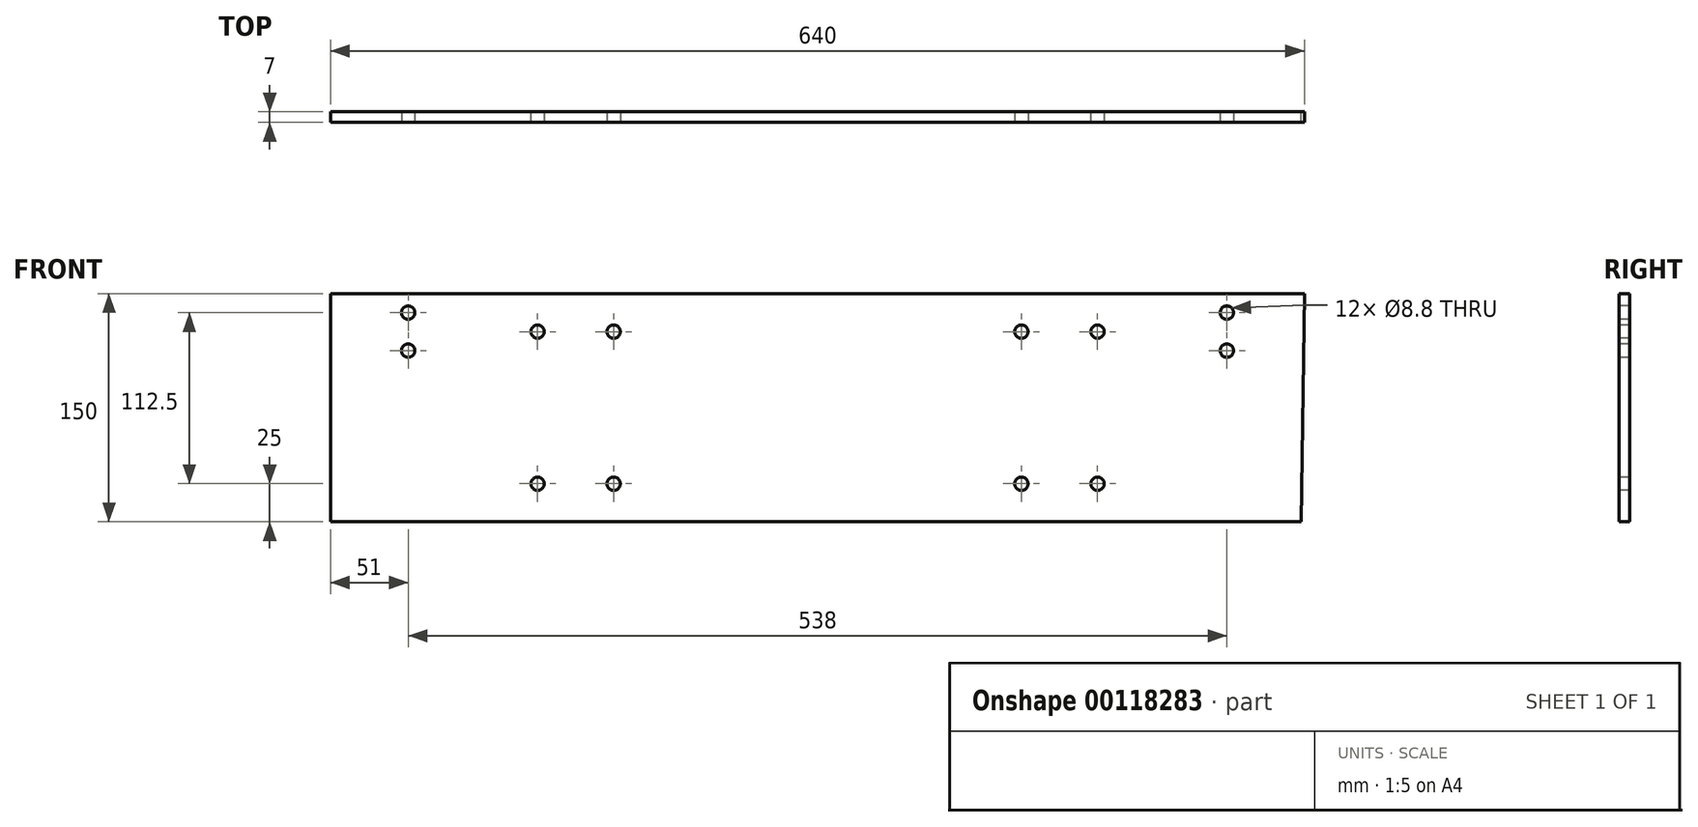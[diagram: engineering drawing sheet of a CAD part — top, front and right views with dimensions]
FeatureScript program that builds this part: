
annotation { "Feature Type Name" : "Feature", "Feature Type Description" : "" }
export const myFeature = defineFeature(function(context is Context, id is Id, definition is map)
    precondition{}
    {
        {
            var Q0;
            Q0=qCreatedBy(makeId("Front.planeOp"),FACE);
            var sketch = newSketch(context, id + "F0", { "sketchPlane" : qUnion([Q0])});
            skLineSegment(sketch, "E0.top", {"start": v(319, -450) * mm, "end": v(-319, -450) * mm});
            skPoint(sketch, "E0.middle", {"position": v(0, 0) * mm});
            skLineSegment(sketch, "E1", {"start": v(-319, -450) * mm, "end": v(-319, -300) * mm});
            skLineSegment(sketch, "E2", {"start": v(-319, -300) * mm, "end": v(321, -300) * mm});
            skLineSegment(sketch, "E3", {"start": v(321, -300) * mm, "end": v(319, -450) * mm});
            skLineSegment(sketch, "E4", {"start": v(-319, -300) * mm, "end": v(-308, -300) * mm});
            skLineSegment(sketch, "E5", {"start": v(-308, -300) * mm, "end": v(-308, -450) * mm});
            skLineSegment(sketch, "E6", {"start": v(321, -300) * mm, "end": v(310, -300) * mm});
            skLineSegment(sketch, "E7", {"start": v(310, -300) * mm, "end": v(310, -450) * mm});
            skSolve(sketch);
        }
        {
            var Q0;
            Q0=makeQuery(id+"F0.imprint","IMPRINT",FACE,{"disambiguationData":[TD([[makeQuery(id+"F0.imprint","IMPRINT",EDGE,{"derivedFrom":sQuery(id+"F0.wireOp",EDGE,"E2")}),-1.0]])]});
            extrude(context, id + "F1", {"entities" : qUnion([Q0]), "depth" : 7 * mm});
        }
        {
            var Q0;
            Q0=makeQuery(id+"F1.opExtrude","CAP_FACE",FACE,{"disambiguationData":[OSD([sQuery(id+"F0.wireOp",EDGE,"E0.top"),sQuery(id+"F0.wireOp",EDGE,"E2"),sQuery(id+"F0.wireOp",EDGE,"E5"),sQuery(id+"F0.wireOp",EDGE,"E7")])],"isStart":false});
            var sketch = newSketch(context, id + "F2", { "sketchPlane" : qUnion([Q0])});
            skLineSegment(sketch, "E8", {"start": v(-308, -300) * mm, "end": v(-158, -300) * mm});
            skLineSegment(sketch, "E9", {"start": v(310, -300) * mm, "end": v(160, -300) * mm});
            skLineSegment(sketch, "E10", {"start": v(160, -300) * mm, "end": v(-158, -300) * mm});
            skLineSegment(sketch, "E11.MirrorCS", {"start": v(198, -300) * mm, "end": v(-208, -300) * mm});
            skLineSegment(sketch, "E12.MirrorCS", {"start": v(-308, -300) * mm, "end": v(-208, -300) * mm});
            skLineSegment(sketch, "E13", {"start": v(-158, -300) * mm, "end": v(-158, -450) * mm});
            skLineSegment(sketch, "E14", {"start": v(-158, -450) * mm, "end": v(-208, -450) * mm});
            skLineSegment(sketch, "E15", {"start": v(-158, -450) * mm, "end": v(-128, -450) * mm});
            skLineSegment(sketch, "E16.bottom", {"start": v(-208, -450) * mm, "end": v(-108, -450) * mm});
            skLineSegment(sketch, "E16.top", {"start": v(-208, -400) * mm, "end": v(-108, -400) * mm});
            skLineSegment(sketch, "E16.left", {"start": v(-208, -450) * mm, "end": v(-208, -400) * mm});
            skLineSegment(sketch, "E16.right", {"start": v(-108, -450) * mm, "end": v(-108, -400) * mm});
            skLineSegment(sketch, "E17", {"start": v(-158, -450) * mm, "end": v(-108, -400) * mm});
            skLineSegment(sketch, "E18", {"start": v(-158, -300) * mm, "end": v(-158, -350) * mm});
            skLineSegment(sketch, "E19", {"start": v(-158, -350) * mm, "end": v(-208, -350) * mm});
            skLineSegment(sketch, "E20", {"start": v(-208, -350) * mm, "end": v(-158, -300) * mm});
            skLineSegment(sketch, "E21", {"start": v(-158, -300) * mm, "end": v(-108, -300) * mm});
            skLineSegment(sketch, "E22", {"start": v(-108, -300) * mm, "end": v(-108, -350) * mm});
            skLineSegment(sketch, "E23", {"start": v(-208, -350) * mm, "end": v(-208, -300) * mm});
            skLineSegment(sketch, "E24", {"start": v(-108, -350) * mm, "end": v(-158, -350) * mm});
            skLineSegment(sketch, "E25", {"start": v(-158, -350) * mm, "end": v(-108, -300) * mm});
            skLineSegment(sketch, "E26", {"start": v(-208, -450) * mm, "end": v(-158, -400) * mm});
            skLineSegment(sketch, "E27", {"start": v(160, -300) * mm, "end": v(160, -450) * mm});
            skLineSegment(sketch, "E28", {"start": v(160, -450) * mm, "end": v(160, -400) * mm});
            skLineSegment(sketch, "E29", {"start": v(160, -400) * mm, "end": v(210, -400) * mm});
            skLineSegment(sketch, "E30", {"start": v(210, -400) * mm, "end": v(210, -450) * mm});
            skLineSegment(sketch, "E31", {"start": v(160, -450) * mm, "end": v(210, -400) * mm});
            skLineSegment(sketch, "E32", {"start": v(160, -400) * mm, "end": v(110, -400) * mm});
            skLineSegment(sketch, "E33", {"start": v(110, -400) * mm, "end": v(110, -450) * mm});
            skLineSegment(sketch, "E34", {"start": v(110, -450) * mm, "end": v(160, -400) * mm});
            skLineSegment(sketch, "E35", {"start": v(160, -300) * mm, "end": v(160, -350) * mm});
            skLineSegment(sketch, "E36", {"start": v(160, -350) * mm, "end": v(160, -350) * mm});
            skLineSegment(sketch, "E37", {"start": v(160, -350) * mm, "end": v(160, -300) * mm});
            skLineSegment(sketch, "E38", {"start": v(160, -300) * mm, "end": v(210, -300) * mm});
            skLineSegment(sketch, "E39", {"start": v(210, -300) * mm, "end": v(210, -350) * mm});
            skLineSegment(sketch, "E40", {"start": v(210, -350) * mm, "end": v(160, -350) * mm});
            skLineSegment(sketch, "E41", {"start": v(210, -300) * mm, "end": v(160, -350) * mm});
            skLineSegment(sketch, "E42", {"start": v(160, -450) * mm, "end": v(135, -425) * mm});
            skLineSegment(sketch, "E43", {"start": v(-158, -450) * mm, "end": v(-183, -425) * mm});
            skLineSegment(sketch, "E44", {"start": v(-158, -350) * mm, "end": v(-183, -325) * mm});
            skLineSegment(sketch, "E45", {"start": v(160, -350) * mm, "end": v(160, -325) * mm});
            skLineSegment(sketch, "E46", {"start": v(210, -350) * mm, "end": v(185, -325) * mm});
            skLineSegment(sketch, "E47", {"start": v(210, -450) * mm, "end": v(185, -425) * mm});
            skLineSegment(sketch, "E48", {"start": v(-108, -450) * mm, "end": v(-133, -425) * mm});
            skLineSegment(sketch, "E49", {"start": v(-108, -350) * mm, "end": v(-133, -325) * mm});
            skLineSegment(sketch, "E50", {"start": v(160, -300) * mm, "end": v(110, -300) * mm});
            skLineSegment(sketch, "E51", {"start": v(160, -350) * mm, "end": v(110, -350) * mm});
            skLineSegment(sketch, "E52", {"start": v(110, -350) * mm, "end": v(110, -300) * mm});
            skLineSegment(sketch, "E53", {"start": v(160, -350) * mm, "end": v(110, -300) * mm});
            skLineSegment(sketch, "E54", {"start": v(135, -325) * mm, "end": v(160, -300) * mm});
            skSolve(sketch);
        }
        {
            var Q0;
            Q0=sQuery(id+"F2.wireOp",VERTEX,"E44.end");
            var Q1;
            Q1=sQuery(id+"F2.wireOp",VERTEX,"E49.end");
            var Q2;
            Q2=sQuery(id+"F2.wireOp",VERTEX,"E46.end");
            var Q3;
            Q3=sQuery(id+"F2.wireOp",VERTEX,"E47.end");
            var Q4;
            Q4=sQuery(id+"F2.wireOp",VERTEX,"E42.end");
            var Q5;
            Q5=sQuery(id+"F2.wireOp",VERTEX,"E48.end");
            var Q6;
            Q6=sQuery(id+"F2.wireOp",VERTEX,"E43.end");
            var Q7;
            Q7=sQuery(id+"F2.wireOp",VERTEX,"IJQfvNGp-jPv3-fynY-866w-Etbx68AJoQDy.end");
            var Q8;
            Q8=sQuery(id+"F2.wireOp",VERTEX,"E54.start");
            var Q9;
            Q9=makeQuery(id+"F1.opExtrude","SWEPT_BODY",BODY,{"disambiguationData":[OSD([sQuery(id+"F0.wireOp",EDGE,"E0.top"),sQuery(id+"F0.wireOp",EDGE,"E2"),sQuery(id+"F0.wireOp",EDGE,"E5"),sQuery(id+"F0.wireOp",EDGE,"E7")])]});
            hole(context, id + "F3", {"style" : HoleStyle.SIMPLE, "endStyle" : HoleEndStyle.THROUGH, "standardTappedOrClearance" : lookupTablePath({ "standard" : "ISO", "fit" : "Normal", "size" : "M8", "type" : "Clearance" }), "standardBlindInLast" : lookupTablePath({ "fit" : "Standard", "standard" : "ISO", "size" : "M8", "type" : "Clearance" }), "holeDiameter" : 8.8 * mm, "locations" : qUnion([Q0, Q1, Q2, Q3, Q4, Q5, Q6, Q7, Q8]), "scope" : qUnion([Q9]), "isTappedThrough" : true});
        }
        {
            var Q0;
            Q0=makeQuery(id+"F1.opExtrude","CAP_FACE",FACE,{"disambiguationData":[OSD([sQuery(id+"F0.wireOp",EDGE,"E0.top"),sQuery(id+"F0.wireOp",EDGE,"E2"),sQuery(id+"F0.wireOp",EDGE,"E5"),sQuery(id+"F0.wireOp",EDGE,"E7")])],"isStart":false});
            var sketch = newSketch(context, id + "F4", { "sketchPlane" : qUnion([Q0])});
            skLineSegment(sketch, "E55", {"start": v(-183, -325) * mm, "end": v(-133, -325) * mm});
            skLineSegment(sketch, "E56", {"start": v(-133, -325) * mm, "end": v(-133, -300) * mm});
            skLineSegment(sketch, "E57", {"start": v(-183, -325) * mm, "end": v(-183, -300) * mm});
            skLineSegment(sketch, "E58", {"start": v(-308, -300) * mm, "end": v(-308, -350) * mm});
            skLineSegment(sketch, "E59", {"start": v(-308, -350) * mm, "end": v(-238, -350) * mm});
            skLineSegment(sketch, "E60", {"start": v(-238, -350) * mm, "end": v(-238, -300) * mm});
            skLineSegment(sketch, "E61", {"start": v(-238, -300) * mm, "end": v(-308, -300) * mm});
            skLineSegment(sketch, "E62", {"start": v(-308, -300) * mm, "end": v(-298, -300) * mm});
            skLineSegment(sketch, "E63", {"start": v(-298, -300) * mm, "end": v(-298, -350) * mm});
            skLineSegment(sketch, "E64", {"start": v(-298, -325) * mm, "end": v(-238, -350) * mm});
            skLineSegment(sketch, "E65", {"start": v(-298, -325) * mm, "end": v(-238, -300) * mm});
            skLineSegment(sketch, "E66", {"start": v(-268, -312.5) * mm, "end": v(-268, -337.5) * mm});
            skLineSegment(sketch, "E67", {"start": v(310, -300) * mm, "end": v(310, -350) * mm});
            skLineSegment(sketch, "E68", {"start": v(310, -350) * mm, "end": v(240, -350) * mm});
            skLineSegment(sketch, "E69", {"start": v(240, -350) * mm, "end": v(240, -300) * mm});
            skLineSegment(sketch, "E70", {"start": v(240, -300) * mm, "end": v(310, -300) * mm});
            skLineSegment(sketch, "E71", {"start": v(310, -300) * mm, "end": v(300, -300) * mm});
            skLineSegment(sketch, "E72", {"start": v(300, -300) * mm, "end": v(300, -350) * mm});
            skLineSegment(sketch, "E73", {"start": v(300, -325) * mm, "end": v(240, -350) * mm});
            skLineSegment(sketch, "E74", {"start": v(240, -300) * mm, "end": v(300, -325) * mm});
            skLineSegment(sketch, "E75", {"start": v(270, -337.5) * mm, "end": v(270, -312.5) * mm});
            skSolve(sketch);
        }
        {
            var Q0;
            Q0=sQuery(id+"F4.wireOp",VERTEX,"E66.end");
            var Q1;
            Q1=sQuery(id+"F4.wireOp",VERTEX,"E66.start");
            var Q2;
            Q2=sQuery(id+"F4.wireOp",VERTEX,"E75.start");
            var Q3;
            Q3=sQuery(id+"F4.wireOp",VERTEX,"E75.end");
            var Q4;
            Q4=makeQuery(id+"F1.opExtrude","SWEPT_BODY",BODY,{"disambiguationData":[OSD([sQuery(id+"F0.wireOp",EDGE,"E0.top"),sQuery(id+"F0.wireOp",EDGE,"E2"),sQuery(id+"F0.wireOp",EDGE,"E5"),sQuery(id+"F0.wireOp",EDGE,"E7")])]});
            hole(context, id + "F5", {"style" : HoleStyle.SIMPLE, "endStyle" : HoleEndStyle.THROUGH, "standardTappedOrClearance" : lookupTablePath({ "standard" : "ISO", "fit" : "Normal", "size" : "M8", "type" : "Clearance" }), "standardBlindInLast" : lookupTablePath({ "fit" : "Standard", "standard" : "ISO", "size" : "M8", "type" : "Clearance" }), "holeDiameter" : 8.8 * mm, "locations" : qUnion([Q0, Q1, Q2, Q3]), "scope" : qUnion([Q4]), "isTappedThrough" : true});
        }
    });
